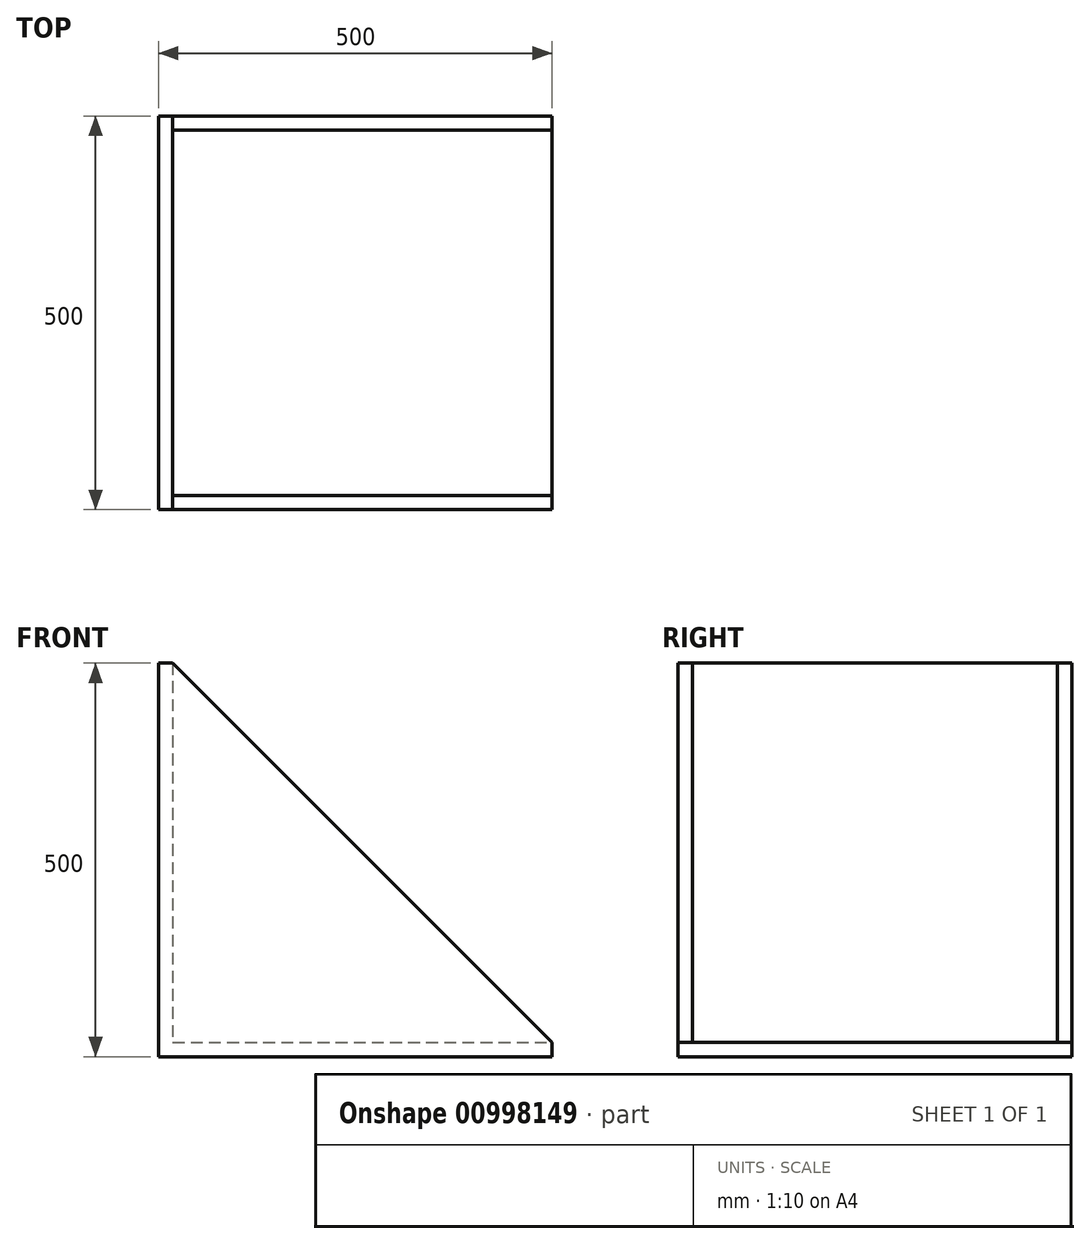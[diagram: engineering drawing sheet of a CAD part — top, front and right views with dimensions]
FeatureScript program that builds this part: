
annotation { "Feature Type Name" : "Feature", "Feature Type Description" : "" }
export const myFeature = defineFeature(function(context is Context, id is Id, definition is map)
    precondition{}
    {
        {
            var Q0;
            Q0=qCreatedBy(makeId("Front.planeOp"),FACE);
            var sketch = newSketch(context, id + "F0", { "sketchPlane" : qUnion([Q0])});
            skLineSegment(sketch, "E0", {"start": v(-216.17, 183.94) * mm, "end": v(-216.17, -316.06) * mm});
            skLineSegment(sketch, "E1", {"start": v(-216.17, -316.06) * mm, "end": v(283.83, -316.06) * mm});
            skLineSegment(sketch, "E2", {"start": v(283.83, -316.06) * mm, "end": v(283.83, -298.06) * mm});
            skLineSegment(sketch, "E3", {"start": v(283.83, -298.06) * mm, "end": v(-198.17, 183.94) * mm});
            skLineSegment(sketch, "E4", {"start": v(-198.17, 183.94) * mm, "end": v(-216.17, 183.94) * mm});
            skLineSegment(sketch, "E5.bottom", {"start": v(-198.17, 183.94) * mm, "end": v(283.83, 183.94) * mm});
            skLineSegment(sketch, "E5.top", {"start": v(-198.17, -298.06) * mm, "end": v(283.83, -298.06) * mm});
            skLineSegment(sketch, "E5.left", {"start": v(-198.17, 183.94) * mm, "end": v(-198.17, -298.06) * mm});
            skLineSegment(sketch, "E5.right", {"start": v(283.83, 183.94) * mm, "end": v(283.83, -298.06) * mm});
            skSolve(sketch);
        }
        {
            var Q0;
            Q0=makeQuery(id+"F0.imprint","IMPRINT",FACE,{"disambiguationData":[TD([[makeQuery(id+"F0.imprint","IMPRINT",EDGE,{"derivedFrom":sQuery(id+"F0.wireOp",EDGE,"E0")}),1.0]])]});
            var Q1;
            Q1=makeQuery(id+"F0.imprint","IMPRINT",FACE,{"disambiguationData":[TD([[makeQuery(id+"F0.imprint","IMPRINT",EDGE,{"derivedFrom":sQuery(id+"F0.wireOp",EDGE,"E3")}),1.0]])]});
            extrude(context, id + "F1", {"entities" : qUnion([Q0, Q1]), "endBound" : BoundingType.SYMMETRIC, "depth" : 500 * mm, "offsetDistance" : 25.4 * mm});
        }
        {
            var Q0;
            {var subQ0=sQuery(id+"F0.wireOp",EDGE,"E5.right");Q0=makeQuery(id+"F0.imprint","IMPRINT",FACE,{"disambiguationData":[TD([[makeQuery(id+"F0.imprint","IMPRINT",EDGE,{"derivedFrom":subQ0}),-1.0]])]});}
            var Q1;
            {var subQ0=sQuery(id+"F0.wireOp",EDGE,"E5.top");Q1=makeQuery(id+"F0.imprint","IMPRINT",FACE,{"disambiguationData":[TD([[makeQuery(id+"F0.imprint","IMPRINT",EDGE,{"derivedFrom":subQ0}),1.0]])]});}
            extrude(context, id + "F2", {"entities" : qUnion([Q0, Q1]), "operationType" : NewBodyOperationType.REMOVE, "endBound" : BoundingType.SYMMETRIC, "oppositeDirection" : true, "depth" : 464 * mm, "offsetDistance" : 25.4 * mm});
        }
    });
